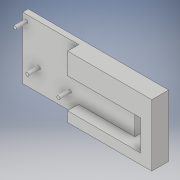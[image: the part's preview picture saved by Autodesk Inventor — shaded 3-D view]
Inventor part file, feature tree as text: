
AUTODESK INVENTOR PART (.ipt)
format: ipt  version: 2017 (Build 210142000, 142)  size: 146,432 bytes
history: native  units: in
note: dims shown in document units (in); Inventor stores cm internally (conversion verified against a paired STEP export)
features: extrude x5, sketch x5
ambient origin geometry x8: Origin, YZ Plane, XZ Plane, XY Plane, X Axis, Y Axis, Z Axis, Center Point
bodies: Solid1 (feature_tree)
feature tree (10):
  extrude  "Extrusion1"  Depth=2.1654in
  extrude  "Extrusion2"  Depth=0.9843in
  extrude  "Extrusion3"  Depth=1.9685in
  extrude  "Extrusion4"  Depth=1.9685in
  extrude  "Extrusion5"  Depth=0.5906in
  sketch  "Sketch3"  dims[d0=4.9213in d1=2.1654in]
  sketch  "Sketch6"  dims[d2=0.1969in d3=0.0in d4=0.9843in]
  sketch  "Sketch7"  dims[d5=0.9843in d6=1.9685in]
  sketch  "Sketch8"  dims[d7=1.9685in d8=0.1181in]
  sketch  "Sketch9"  dims[d9=0.126in d10=0.6575in d11=90.0deg d12=0.563in d13=0.3189in d14=0.4921in d15=0.1142in d16=0.1142in d17=0.1142in d18=0.3937in d19=0.0in d20=2.9528in d21=0.3937in d22=0.0in d23=0.3543in d24=2.5591in d25=1.063in d26=0.3937in d27=0.0in d28=0.5906in d29=0.7874in d30=0.0in]
